# Revit family: Hager-IC-Flush_mounted-IP30-Without_Cover-With_DIN-Hosted-PL-en
name_source: partatom
category: Electrical Equipment
units: mm (PartAtom-declared; Revit-internal decimal feet)

## family parameters
Cut with Voids When Loaded = No
Host = Face
Maintain Annotation Orientation = Yes
Panel Configuration = Two Columns, Circuits Across
Part Type = Panelboard
Room Calculation Point = No
Round Connector Dimension = Use Diameter
Shared = No

## types (4) — shared parameters
BC_MODEL_ID = 1554354
BC_OBJECT_ID = 513887
BC_OBJECT_VERSION = #5
Code hager = ADD-EC000214_EU
EF000003 - Mounting method = Flush-mounted
EF000007 - Colour = White
EF000024 - UV resistant = No
EF000116 - RAL-number = 9010
EF000118 - With mounting plate = No
EF000218 - Built-in depth = 72 mm  [stored 0.23622 ft]
EF001062 - EMC-version = No
EF001088 - Extension possible = Yes
EF001134 - DIN-rail = Yes
EF004462 - Type of closure = Other
EF005474 - Degree of protection (IP) = IP30
EF006244 - Transparent cover/door = No
EF006306 - With lock = No
EF009212 - Cover model = Closed
EF015776 - Earthing terminal block = Yes
EF015777 - Neutral terminal block = Yes
EF015941 - Signal passing door = Yes
ETIM class code = EC000214
ETIM class name = Small distribution board
HG000001-Number of columns = 1
HG000002-With door or cover = No
HG000003-Range = IC
HG000005-Thickness = 2 mm  [stored 0.00656168 ft]
HG000006-Flush mounted = Yes
HG000009-Double swing door = No
HG000010-Asymmetric doors = No
HG000011-Empty rows from bottom = No
HG000012-Door swing angle = 90.00°
HG000013-Door on the left = No
HG000014-Door on the right = Yes
HG000015-Clearance visibility = Yes
HG000016-Door 3D visibility = Yes
HG000017-Distance between poles = 18 mm  [stored 0.0590551 ft]
HG000060-RAL-number = 9010
HG000099-Onfly Template ID = 507532
Manufacturer = Hager
Name = IC-Flush_mounted-IP30-Without_Cover-With_DIN-PL
Name BIM&CO = Electricity
Name hager = ADD_Enclosures_EC000214
Uniformat = Low Tension Service & Dist.
Uniformat code = D501001
zero-valued in all types: Default Elevation, EF001131 - Inner depth, HG000007-Number of empty columns, HG000008-Number of empty rows

## per-type parameters (varying)
| type | BC_VARIANT_ID | EF000008 - Width | EF000040 - Height | EF000049 - Depth | EF000266 - Number of rows | EF000332 - Built-in height | EF000846 - Built-in width | EF002950 - Width in number of modular spacings | HG000004-Manufacturer reference | HGEF000266-Number of rows | HGEF002950-Width in number of modular spacings |
| IC-Flush_mounted_W236_H206_D91_8_Modular_Spacing-VR108NP | 1178953 | 236 mm | 206 mm  [stored 0.675853 ft] | 91 mm  [stored 0.298556 ft] | 1 | 188 mm  [stored 0.616798 ft] | 218 mm  [stored 0.715223 ft] | 8 | VR108NP | 1 | 8 |
| IC-Flush_mounted_W308_H226_D91_12_Modular_Spacing-VR112NP | 1178954 | 308 mm  [stored 1.0105 ft] | 226 mm  [stored 0.74147 ft] | 91 mm  [stored 0.298556 ft] | 1 | 208 mm | 290 mm  [stored 0.951444 ft] | 12 | VR112NP | 1 | 12 |
| IC-Flush_mounted_W416_H226_D91_18_Modular_Spacing-VR118NP | 1178955 | 416 mm | 226 mm  [stored 0.74147 ft] | 91 mm  [stored 0.298556 ft] | 1 | 208 mm | 398 mm  [stored 1.30577 ft] | 18 | VR118NP | 1 | 18 |
| IC-Flush_mounted_W308_H351_D93_12_Modular_Spacing-VR212NP | 1178956 | 308 mm  [stored 1.0105 ft] | 351 mm  [stored 1.15157 ft] | 93 mm  [stored 0.305118 ft] | 2 | 333 mm  [stored 1.09252 ft] | 290 mm  [stored 0.951444 ft] | 12 | VR212NP | 2 | 12 |

note: column(s) folded — value = type name in every type: Reference

note: [stored X ft] marks values corroborated as IEEE doubles in the binary element streams (Revit-internal decimal feet)

## geometry (parser evidence)
native form markers: Sweep x14
no freeform markers — native parametric forms only
